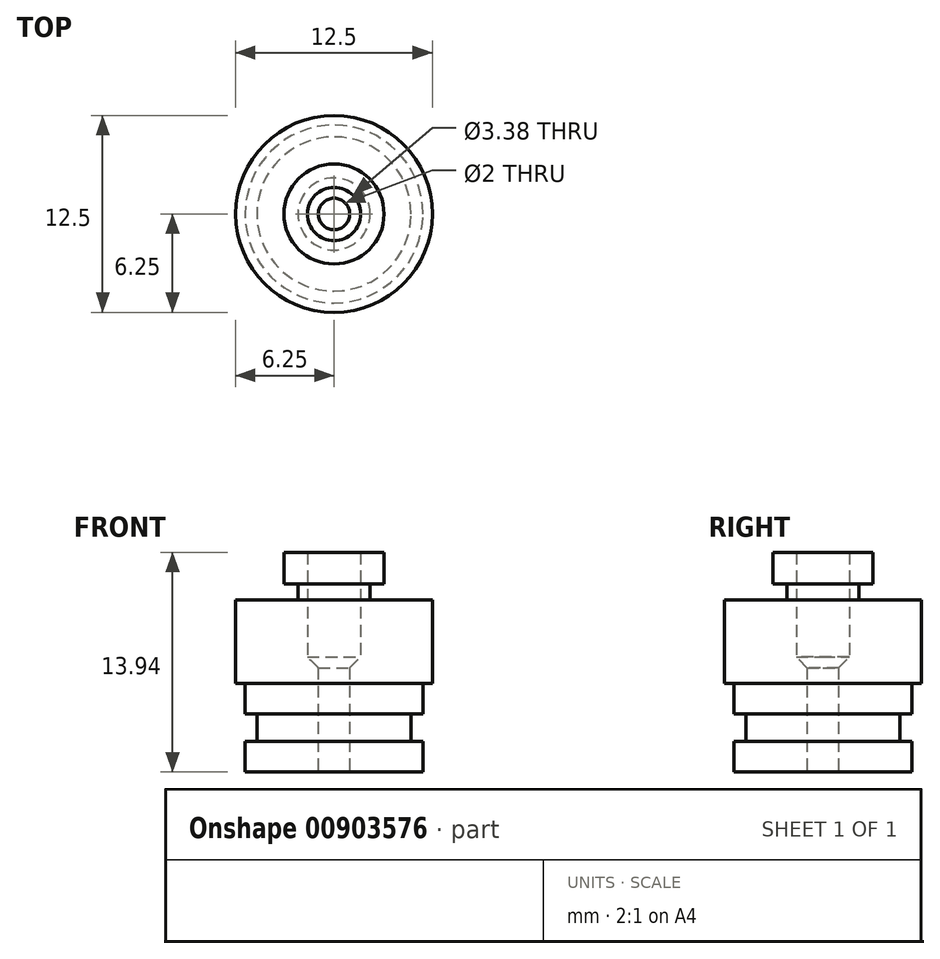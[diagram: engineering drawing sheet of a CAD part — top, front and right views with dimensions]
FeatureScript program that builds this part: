
annotation { "Feature Type Name" : "Feature", "Feature Type Description" : "" }
export const myFeature = defineFeature(function(context is Context, id is Id, definition is map)
    precondition{}
    {
        {
            var Q0;
            Q0=qCreatedBy(makeId("Front.planeOp"),FACE);
            var sketch = newSketch(context, id + "F0", { "sketchPlane" : qUnion([Q0])});
            skLineSegment(sketch, "E0", {"start": v(1, 0) * mm, "end": v(5.65, 0) * mm});
            skLineSegment(sketch, "E1", {"start": v(6.25, 5.62) * mm, "end": v(6.25, 10.94) * mm});
            skLineSegment(sketch, "E2", {"start": v(3.18, 13.94) * mm, "end": v(1.69, 13.94) * mm});
            skLineSegment(sketch, "E3", {"start": v(1.69, 6.62) * mm, "end": v(1, 6.62) * mm, "construction": true});
            skLineSegment(sketch, "E4", {"start": v(1, 6.62) * mm, "end": v(1, 0) * mm});
            skLineSegment(sketch, "E5", {"start": v(3.18, 11.94) * mm, "end": v(3.18, 13.94) * mm});
            skLineSegment(sketch, "E6", {"start": v(1.69, 13.94) * mm, "end": v(1.69, 7.3) * mm});
            skLineSegment(sketch, "E7", {"start": v(0, 0) * mm, "end": v(0, 19.93) * mm, "construction": true});
            skLineSegment(sketch, "E8", {"start": v(6.25, 10.94) * mm, "end": v(2.29, 10.94) * mm});
            skLineSegment(sketch, "E9", {"start": v(2.29, 10.94) * mm, "end": v(2.29, 11.94) * mm});
            skLineSegment(sketch, "E10", {"start": v(2.29, 11.94) * mm, "end": v(3.18, 11.94) * mm});
            skLineSegment(sketch, "E11", {"start": v(5.65, 0) * mm, "end": v(5.65, 1.94) * mm});
            skLineSegment(sketch, "E12", {"start": v(5.65, 5.62) * mm, "end": v(6.25, 5.62) * mm});
            skLineSegment(sketch, "E13", {"start": v(5.65, 1.94) * mm, "end": v(4.9, 1.94) * mm});
            skLineSegment(sketch, "E14", {"start": v(4.9, 1.94) * mm, "end": v(4.9, 3.69) * mm});
            skLineSegment(sketch, "E15", {"start": v(4.9, 3.69) * mm, "end": v(5.65, 3.69) * mm});
            skLineSegment(sketch, "E16.trimOffspring", {"start": v(5.65, 3.69) * mm, "end": v(5.65, 5.62) * mm});
            skCircle(sketch, "E17", {"center": v(0, 7.87) * mm, "radius": 1.59 * mm, "construction": true});
            skLineSegment(sketch, "E18", {"start": v(1, 6.62) * mm, "end": v(1.69, 7.3) * mm});
            skLineSegment(sketch, "E19", {"start": v(0, 8.93) * mm, "end": v(1.18, 8.93) * mm, "construction": true});
            skSolve(sketch);
        }
        {
            var Q0;
            Q0 = qSketchRegion(id + "F0", true);
            var Q1;
            Q1=sQuery(id+"F0.wireOp",EDGE,"E7");
            revolve(context, id + "F1", {"surfaceOperationType" : NewSurfaceOperationType.NEW, "entities" : qUnion([Q0]), "axis" : qUnion([Q1]), "revolveType" : RevolveType.FULL});
        }
    });
